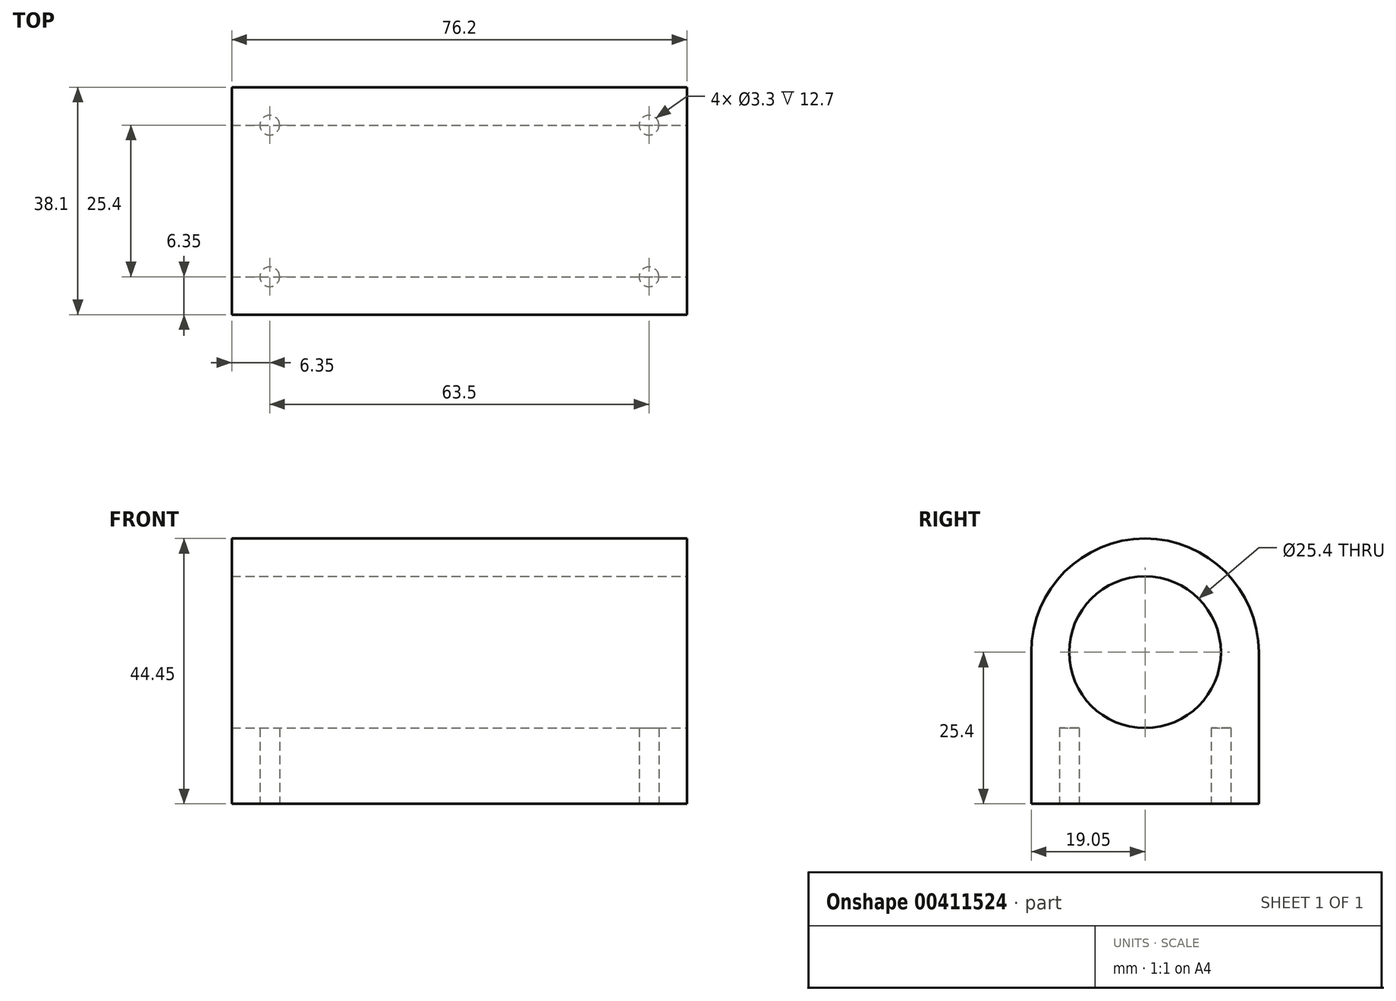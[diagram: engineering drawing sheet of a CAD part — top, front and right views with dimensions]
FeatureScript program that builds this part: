
annotation { "Feature Type Name" : "Feature", "Feature Type Description" : "" }
export const myFeature = defineFeature(function(context is Context, id is Id, definition is map)
    precondition{}
    {
        {
            var Q0;
            Q0=qCreatedBy(makeId("Right.planeOp"),FACE);
            var sketch = newSketch(context, id + "F0", { "sketchPlane" : qUnion([Q0])});
            skLineSegment(sketch, "E0", {"start": v(19.05, 0) * mm, "end": v(19.05, -25.4) * mm});
            skLineSegment(sketch, "E1", {"start": v(19.05, -25.4) * mm, "end": v(-19.05, -25.4) * mm});
            skLineSegment(sketch, "E2", {"start": v(-19.05, -25.4) * mm, "end": v(-19.05, 0) * mm});
            skArc(sketch, "E3", {"start": v(19.05, 0) * mm, "mid": v(0, 19.05) * mm, "end": v(-19.05, 0) * mm});
            skSolve(sketch);
        }
        {
            var Q0;
            Q0 = qSketchRegion(id + "F0", true);
            extrude(context, id + "F1", {"entities" : qUnion([Q0]), "endBound" : BoundingType.SYMMETRIC, "depth" : 76.2 * mm, "hasSecondDirection" : true, "secondDirectionOppositeDirection" : true, "secondDirectionDepth" : 25.4 * mm});
        }
        {
            var Q0;
            Q0=makeQuery(id+"F1.opExtrude","CAP_FACE",FACE,{"disambiguationData":[OSD([sQuery(id+"F0.wireOp",EDGE,"E0"),sQuery(id+"F0.wireOp",EDGE,"E1"),sQuery(id+"F0.wireOp",EDGE,"E2"),sQuery(id+"F0.wireOp",EDGE,"E3")])],"isStart":false});
            var sketch = newSketch(context, id + "F2", { "sketchPlane" : qUnion([Q0])});
            skCircle(sketch, "E4", {"center": v(0, 0) * mm, "radius": 12.7 * mm});
            skSolve(sketch);
        }
        {
            var Q0;
            Q0 = qSketchRegion(id + "F2", true);
            extrude(context, id + "F3", {"entities" : qUnion([Q0]), "operationType" : NewBodyOperationType.REMOVE, "endBound" : BoundingType.SYMMETRIC, "oppositeDirection" : true, "depth" : 508 * mm});
        }
        {
            var Q0;
            Q0=makeQuery(id+"F1.opExtrude","SWEPT_FACE",FACE,{"disambiguationData":[OSD([sQuery(id+"F0.wireOp",EDGE,"E1")])]});
            var sketch = newSketch(context, id + "F4", { "sketchPlane" : qUnion([Q0])});
            skCircle(sketch, "E5", {"center": v(-31.75, 12.7) * mm, "radius": 1.65 * mm});
            skCircle(sketch, "E6", {"center": v(-31.75, -12.7) * mm, "radius": 1.65 * mm});
            skCircle(sketch, "E7", {"center": v(31.75, -12.7) * mm, "radius": 1.65 * mm});
            skCircle(sketch, "E8", {"center": v(31.75, 12.7) * mm, "radius": 1.65 * mm});
            skSolve(sketch);
        }
        {
            var Q0;
            Q0 = qSketchRegion(id + "F4", true);
            extrude(context, id + "F5", {"entities" : qUnion([Q0]), "operationType" : NewBodyOperationType.REMOVE, "oppositeDirection" : true, "depth" : 12.7 * mm});
        }
    });
